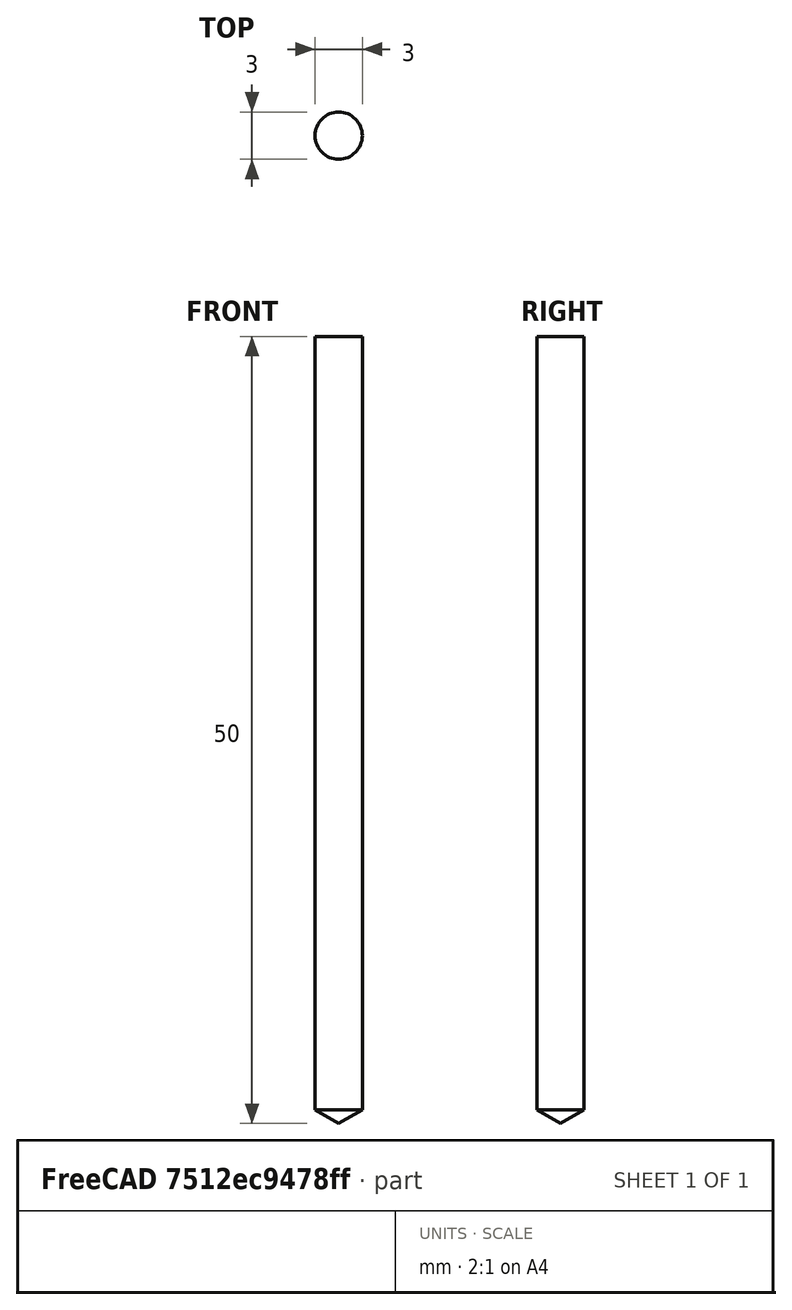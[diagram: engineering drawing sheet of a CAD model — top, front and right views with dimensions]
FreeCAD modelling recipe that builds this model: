
FCSTD DOCUMENT  (FreeCAD 0.21R32460 (Git))
Label: drill
License: Creative Commons Attribution 4.0
LicenseURL: https://creativecommons.org/licenses/by/4.0/
objects: Sketcher::SketchObject×1, PartDesign::Revolution×1, App::FeaturePython×1, PartDesign::Body×1
note: 4 computed .brp shape members not serialized (recipe doc carries the construction recipe); baked Part::Feature solids carry a one-line shape summary decoded from their .brp

FEATURE [Sketcher::SketchObject] Sketch
  FullyConstrained = true
  MapMode = 5
  Placement = pos=(0,0,0) rot=(1,0,0;1.5708rad)
  Support = -> [XZ_Plane]
  expr: Constraints[13] = <<Attributes>>.TipAngle
  expr: Constraints[14] = <<Attributes>>.Diameter
  expr: Constraints[15] = <<Attributes>>.Length
  sketch-geometry (7):
    g0: LineSegment StartX=0 StartY=50 StartZ=0 EndX=0 EndY=0 EndZ=0
    g1: LineSegment StartX=0 StartY=0 StartZ=0 EndX=1.5 EndY=0.883568 EndZ=0
    g2: LineSegment StartX=1.5 StartY=0.883568 StartZ=0 EndX=1.5 EndY=50 EndZ=0
    g3: LineSegment StartX=1.5 StartY=50 StartZ=0 EndX=0 EndY=50 EndZ=0
    g4: LineSegment StartX=1.5 StartY=0.883568 StartZ=0 EndX=-1.5 EndY=0.883568 EndZ=0
    g5: LineSegment StartX=-1.5 StartY=0.883568 StartZ=0 EndX=0 EndY=0 EndZ=0
    g6: LineSegment StartX=0 StartY=0 StartZ=0 EndX=1.5 EndY=0.883568 EndZ=0
  constraints (17):
    c: Vertical(g0)
    c: Coincident(g0,g1)
    c: Coincident(g1,g2)
    c: Vertical(g2)
    c: Coincident(g2,g3)
    c: Horizontal(g3)
    c: Coincident(g0,g3)
    c: Coincident(g4,g5)
    c: Coincident(g5,g6)
    c: Coincident(g6,g4)
    c: Coincident(g1,g4)
    c: Coincident(g5,g0)
    c: Symmetric(g4,g1,g0)
    c: Angle(g1,g5) = 2.07694
    c: DistanceX(g4,g4) = 3
    c: DistanceY(g0,g0) = 50
    c: Coincident(g0,g-1)
FEATURE [PartDesign::Revolution] Revolution
  AllowMultiFace = false
  Angle = 360
  Axis = (0,-2e-16,1)
  Base = (0,0,0)
  Placement = pos=(0,0,0) rot=(1,0,0;1.5708rad)
  Profile = -> Sketch
  ReferenceAxis = -> Sketch [V_Axis]
  Reversed = true
FEATURE [App::FeaturePython] PropertyBag  label="Attributes"  # WARN: FeaturePython — macro-defined, semantics opaque (R4)
  Chipload = 0
  CustomPropertyGroups = Attributes | Shape
  Diameter = 3
  Flutes = 0
  Length = 50
  Material = 0
  TipAngle = 119
FEATURE [PartDesign::Body] Body  label="Drill"
  Group = -> [Sketch,Revolution,PropertyBag]
  Origin = -> Origin
  Tip = -> Revolution
